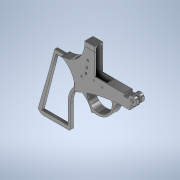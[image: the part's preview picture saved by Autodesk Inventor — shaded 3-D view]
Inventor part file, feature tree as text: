
AUTODESK INVENTOR PART (.ipt)
format: ipt  version: 2021 (Build 250183000, 183)  size: 564,224 bytes
history: native  units: in
note: dims shown in document units (in); Inventor stores cm internally (conversion verified against a paired STEP export)
features: extrude x31, sketch x26, projected_geometry x5, other x3, fillet x2, mirror x1, chamfer x1
ambient origin geometry x8: Origin, YZ Plane, XZ Plane, XY Plane, X Axis, Y Axis, Z Axis, Center Point
bodies: Solid1 (feature_tree)
feature tree (69):
  sketch  "Sketch1"  dims[d1=2.7165in d2=1.7717in]
  extrude  "Extrusion1"  Depth=2.7165in
  extrude  "Extrusion2"  Depth=1.1524in
  extrude  "Extrusion4"  Depth=0.3228in
  extrude  "Extrusion6"  Depth=0.0587in
  extrude  "Extrusion8"  Depth=1.0197in
  extrude  "Extrusion9"  Depth=0.3937in
  extrude  "Extrusion10"  Depth=0.9488in
  sketch  "Sketch4"  dims[d5=0.3228in d6=1.0378in]
  extrude  "Extrusion17"  Depth=0.8256in
  extrude  "Extrusion18"  Depth=0.8255in
  extrude  "Extrusion19"  Depth=0.0787in
  fillet  "Arredondamento1"  Radius=5.1447in
  extrude  "Extrusão20"  Depth=0.0787in
  extrude  "Extrusão21"  Depth=0.0394in
  extrude  "Extrusão22"  Depth=0.3937in
  mirror  "Espelhamento1"
  sketch  "Esboço10"  dims[d15=1.637in d16=0.8256in]
  extrude  "Extrusão24"  Depth=0.3112in
  extrude  "Extrusão27"  Depth=0.3535in TaperAngle=0.0deg
  extrude  "Extrusion29"  Depth=0.3535in TaperAngle=0.0deg
  extrude  "Extrusion30"  Depth=0.3535in
  extrude  "Extrusion31"  Depth=0.5906in TaperAngle=0.0deg
  extrude  "Extrusion34"  Depth=0.3535in TaperAngle=0.0deg
  extrude  "Extrusion33"  TaperAngle=0.0deg  [1 undecoded]
  chamfer  "Chamfer2"  Distance=0.315in
  extrude  "Extrusão37"  Depth=0.0787in TaperAngle=0.0deg
  fillet  "Arredondamento3"  Radius=0.098in
  extrude  "Extrusão39"  Depth=0.1181in TaperAngle=0.0deg
  other  "Plano de trabalho4"
  extrude  "Extrusão40"  Depth=0.0787in
  extrude  "Extrusão41"  Depth=0.1181in
  extrude  "Extrusão42"  Depth=0.1768in
  extrude  "Extrusão43"  Depth=0.0787in
  extrude  "Extrusão44"  Depth=0.3937in
  extrude  "Extrusão45"  Depth=0.3937in
  extrude  "Extrusão47"  Depth=0.3937in TaperAngle=0.0deg
  extrude  "Extrusão48"  Depth=0.3937in
  extrude  "Extrusão49"  Depth=0.3937in TaperAngle=0.0deg
  sketch  "Sketch3"  dims[d3=1.7323in d4=1.1524in]
  sketch  "Sketch6"  dims[d7=0.9614in d8=0.0587in]
  sketch  "Esboço7"  dims[d9=1.0197in d10=1.0197in]
  sketch  "Esboço8"  dims[d11=0.3937in d12=0.272in]
  sketch  "Esboço9"  dims[d13=0.7185in d14=0.9488in]
  other  "Contorno projetado1"
  sketch  "Esboço11"  dims[d17=0.9866in d18=0.8255in]
  other  "Contorno projetado2"
  sketch  "Esboço14"  dims[d19=0.5902in d20=0.0787in d21=5.1447in]
  sketch  "Sketch16"  dims[d22=0.0787in d23=0.3543in]
  projected_geometry  "Projected Loop5"
  sketch  "Sketch17"  dims[d24=0.0394in d25=0.0394in]
  projected_geometry  "Projected Loop6"
  sketch  "Sketch18"  dims[d26=0.0787in d27=0.3937in]
  projected_geometry  "Projected Loop7"
  sketch  "Sketch22"  dims[d28=1.811in d29=0.3112in]
  projected_geometry  "Projected Loop10"
  sketch  "Sketch23"  dims[d30=0.1473in d34=0.3535in d35=0.0in]
  projected_geometry  "Projected Loop11"
  sketch  "Esboço26"  dims[d36=0.3535in d37=0.0in d40=0.3543in d41=0.0in]
  sketch  "Esboço29"  dims[d44=0.3535in d45=0.0in d49=0.7185in]
  sketch  "Esboço30"  dims[d50=0.0394in d51=0.0in d52=0.5906in d53=0.0in]
  sketch  "Esboço31"  dims[d54=0.5906in d55=0.0in d76=0.3535in d77=0.0in]
  sketch  "Esboço32"  dims[d78=0.1575in d79=0.0in d80=0.0in d81=0.315in d82=0.0in]
  sketch  "Esboço33"  dims[d83=0.0787in d84=0.098in d85=0.0in d86=0.098in d87=0.0in]
  sketch  "Esboço34"  dims[d88=1.0197in d89=0.1181in d90=0.0in]
  sketch  "Esboço35"  dims[d91=0.0787in d92=0.0787in]
  sketch  "Esboço36"  dims[d93=1.3339in d94=0.1181in]
  sketch  "Esboço37"  dims[d96=0.1768in d97=0.1768in]
  sketch  "Esboço38"  dims[d104=0.4724in d105=0.0in d114=0.0787in d116=0.1959in d117=0.1533in d118=0.1575in d119=0.0in d121=0.2419in d124=0.0709in d125=0.0in d126=0.4644in d127=0.0in d128=0.2756in d129=0.0in d138=0.9055in d139=0.0in d140=0.7874in d141=0.0in d143=0.2362in d153=0.0197in d154=0.0492in d155=45.0deg d156=0.0in d157=0.0in d158=0.3535in d160=0.2756in d162=0.0389in d163=0.5in d164=0.0587in d165=0.0587in d167=0.0394in d170=0.5906in d171=0.6693in d172=0.0in d173=30.0deg d174=0.6693in d175=0.0in d176=0.0709in d177=0.5512in d178=0.0in d179=0.0787in d180=0.6507in d181=0.294in d182=0.5512in d183=0.0in d184=0.3312in d185=0.0in d186=0.0787in d188=0.0591in d189=0.0197in d190=0.0in d191=0.0591in d192=0.0197in d193=0.0in d194=0.0787in d197=0.0197in d198=0.0in d199=0.0787in d200=0.0197in d201=0.0in d202=0.0591in d203=0.0197in d204=0.0in d46=0.3937in d47=0.3937in d48=0.3937in d56=0.2953in d57=0.1476in d115=0.0344in]
note: 1 required parameter value undecoded (feature->parameter linkage not recoverable at this tier; creation-order binding heuristic only, values carry confidence <= 0.55)
